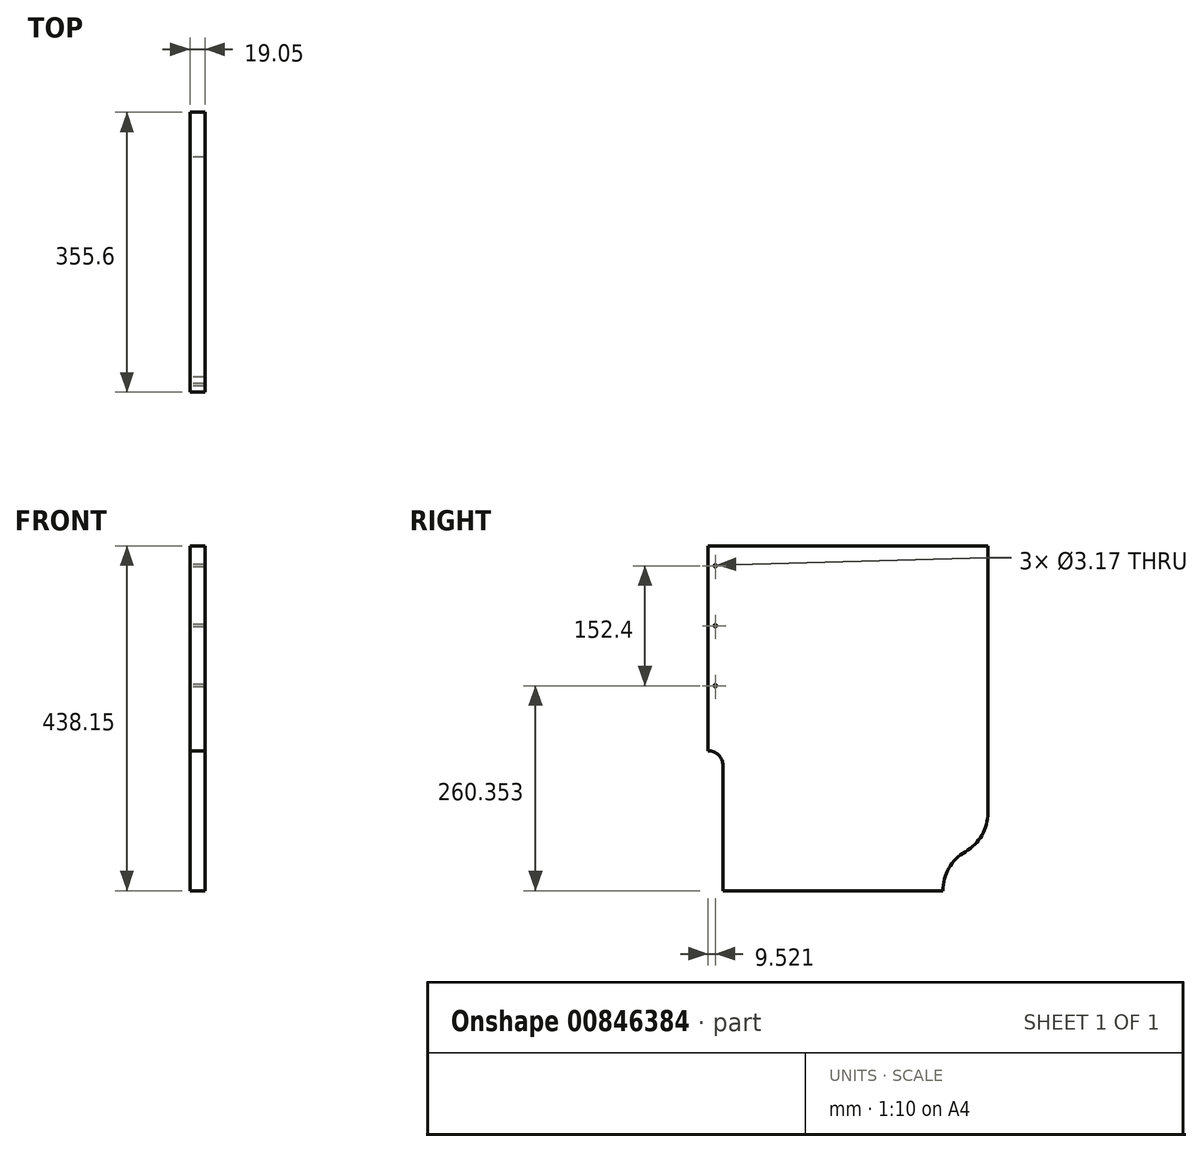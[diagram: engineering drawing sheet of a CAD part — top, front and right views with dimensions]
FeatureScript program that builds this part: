
annotation { "Feature Type Name" : "Feature", "Feature Type Description" : "" }
export const myFeature = defineFeature(function(context is Context, id is Id, definition is map)
    precondition{}
    {
        {
            var Q0;
            Q0=qCreatedBy(makeId("Right.planeOp"),FACE);
            var sketch = newSketch(context, id + "F0", { "sketchPlane" : qUnion([Q0])});
            skLineSegment(sketch, "E0.bottom", {"start": v(-155.23, 276.63) * mm, "end": v(200.37, 276.63) * mm});
            skLineSegment(sketch, "E0.top", {"start": v(-136.18, -161.52) * mm, "end": v(143.22, -161.52) * mm});
            skLineSegment(sketch, "E0.left", {"start": v(-155.23, 276.63) * mm, "end": v(-155.23, 16.28) * mm});
            skLineSegment(sketch, "E0.right", {"start": v(200.37, 276.63) * mm, "end": v(200.37, -62.53) * mm});
            skArc(sketch, "E1", {"start": v(171.8, -112.02) * mm, "mid": v(150.87, -132.94) * mm, "end": v(143.22, -161.52) * mm});
            skLineSegment(sketch, "E2.top", {"start": v(-155.23, 16.28) * mm, "end": v(-155.23, 16.28) * mm});
            skLineSegment(sketch, "E2.right", {"start": v(-136.18, -161.52) * mm, "end": v(-136.18, -2.77) * mm});
            skArc(sketch, "E3.filletArc", {"start": v(-136.18, -2.77) * mm, "mid": v(-141.76, 10.7) * mm, "end": v(-155.23, 16.28) * mm});
            skArc(sketch, "E4.filletArc", {"start": v(171.8, -112.02) * mm, "mid": v(192.7, -91.1) * mm, "end": v(200.37, -62.53) * mm});
            skCircle(sketch, "E5", {"center": v(-145.7, 98.83) * mm, "radius": 1.59 * mm});
            skCircle(sketch, "E6", {"center": v(-145.7, 175.03) * mm, "radius": 1.59 * mm});
            skCircle(sketch, "E7", {"center": v(-145.7, 251.23) * mm, "radius": 1.59 * mm});
            skSolve(sketch);
        }
        {
            var Q0;
            Q0=makeQuery(id+"F0.imprint","IMPRINT",FACE,{"disambiguationData":[TD([[makeQuery(id+"F0.imprint","IMPRINT",EDGE,{"derivedFrom":sQuery(id+"F0.wireOp",EDGE,"E0.bottom")}),-1.0]])]});
            extrude(context, id + "F1", {"entities" : qUnion([Q0]), "depth" : 19.05 * mm, "offsetDistance" : 25.4 * mm});
        }
    });
